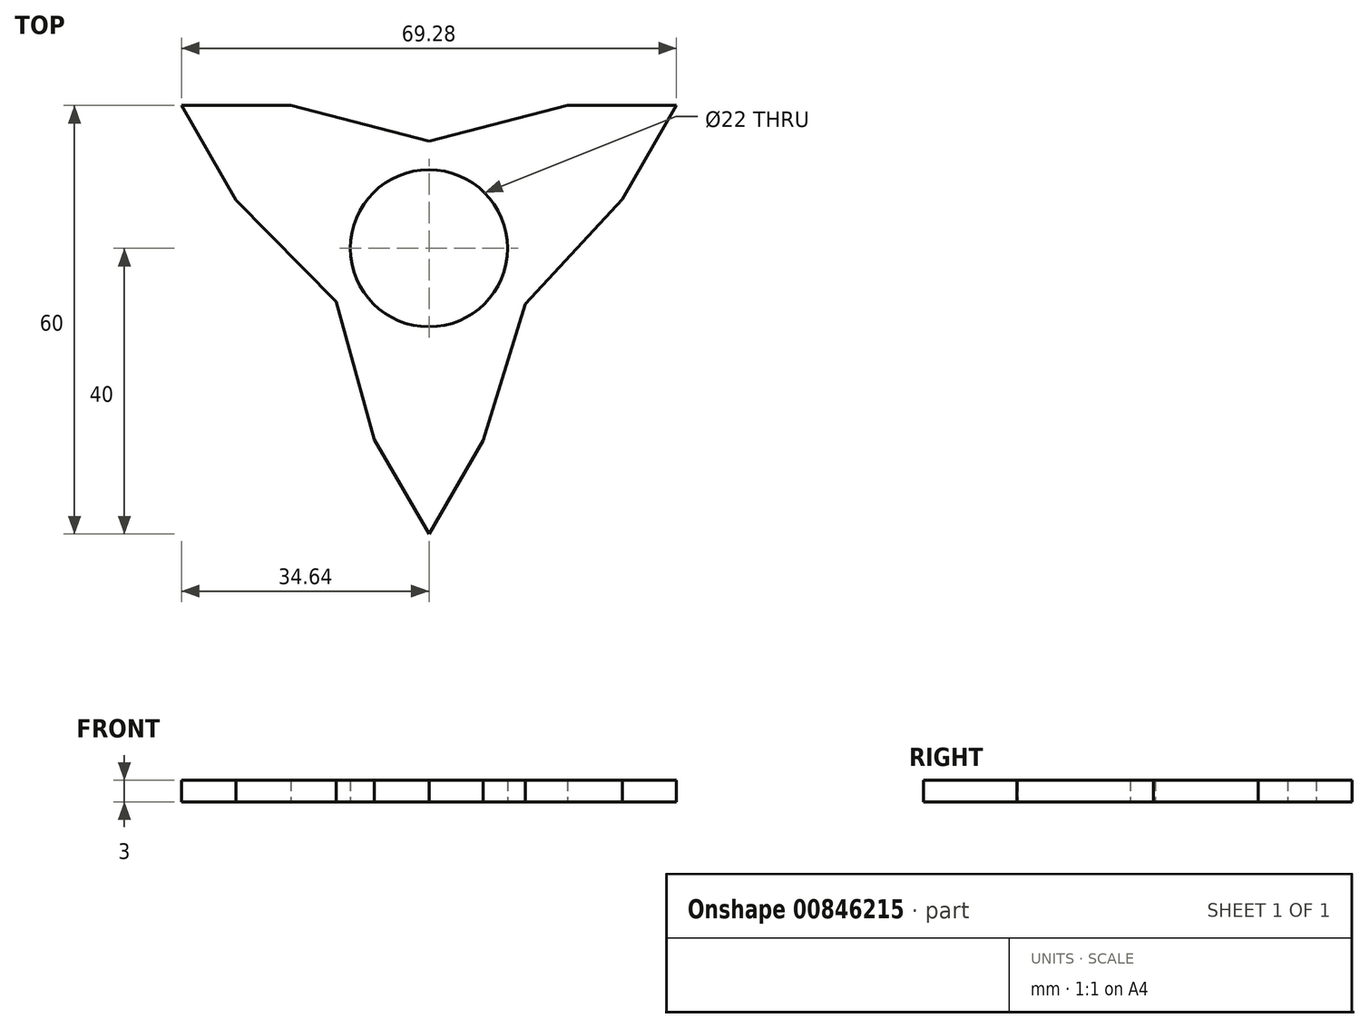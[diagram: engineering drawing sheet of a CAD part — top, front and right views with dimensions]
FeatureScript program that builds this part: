
annotation { "Feature Type Name" : "Feature", "Feature Type Description" : "" }
export const myFeature = defineFeature(function(context is Context, id is Id, definition is map)
    precondition{}
    {
        {
            var Q0;
            Q0=qCreatedBy(makeId("Top.planeOp"),FACE);
            var sketch = newSketch(context, id + "F0", { "sketchPlane" : qUnion([Q0])});
            skCircle(sketch, "E0", {"center": v(0, 0) * mm, "radius": 11 * mm});
            skLineSegment(sketch, "E1.0", {"start": v(-34.64, 20) * mm, "end": v(-19.36, 20) * mm});
            skLineSegment(sketch, "E1.1", {"start": v(34.64, 20) * mm, "end": v(27.07, 6.9) * mm});
            skLineSegment(sketch, "E1.2", {"start": v(0, -40) * mm, "end": v(-7.64, -26.77) * mm});
            skLineSegment(sketch, "E2", {"start": v(13.5, -7.8) * mm, "end": v(27.07, 6.9) * mm});
            skLineSegment(sketch, "E3", {"start": v(13.5, -7.8) * mm, "end": v(7.57, -26.9) * mm});
            skLineSegment(sketch, "E4", {"start": v(0, 15) * mm, "end": v(19.36, 20) * mm});
            skLineSegment(sketch, "E5", {"start": v(0, 15) * mm, "end": v(-19.36, 20) * mm});
            skLineSegment(sketch, "E6", {"start": v(-13, -7.5) * mm, "end": v(-7.64, -26.77) * mm});
            skLineSegment(sketch, "E7", {"start": v(-13, -7.5) * mm, "end": v(-27, 6.77) * mm});
            skLineSegment(sketch, "E8.trimOffspring", {"start": v(19.36, 20) * mm, "end": v(34.64, 20) * mm});
            skLineSegment(sketch, "E9.trimOffspring", {"start": v(-27, 6.77) * mm, "end": v(-34.64, 20) * mm});
            skLineSegment(sketch, "E10.trimOffspring", {"start": v(7.57, -26.9) * mm, "end": v(0, -40) * mm});
            skSolve(sketch);
        }
        {
            var Q0;
            Q0=makeQuery(id+"F0.imprint","IMPRINT",FACE,{"disambiguationData":[TD([[makeQuery(id+"F0.imprint","IMPRINT",EDGE,{"derivedFrom":sQuery(id+"F0.wireOp",EDGE,"E0")}),-1.0]])]});
            extrude(context, id + "F1", {"entities" : qUnion([Q0]), "depth" : 3 * mm, "offsetDistance" : 25 * mm});
        }
    });
